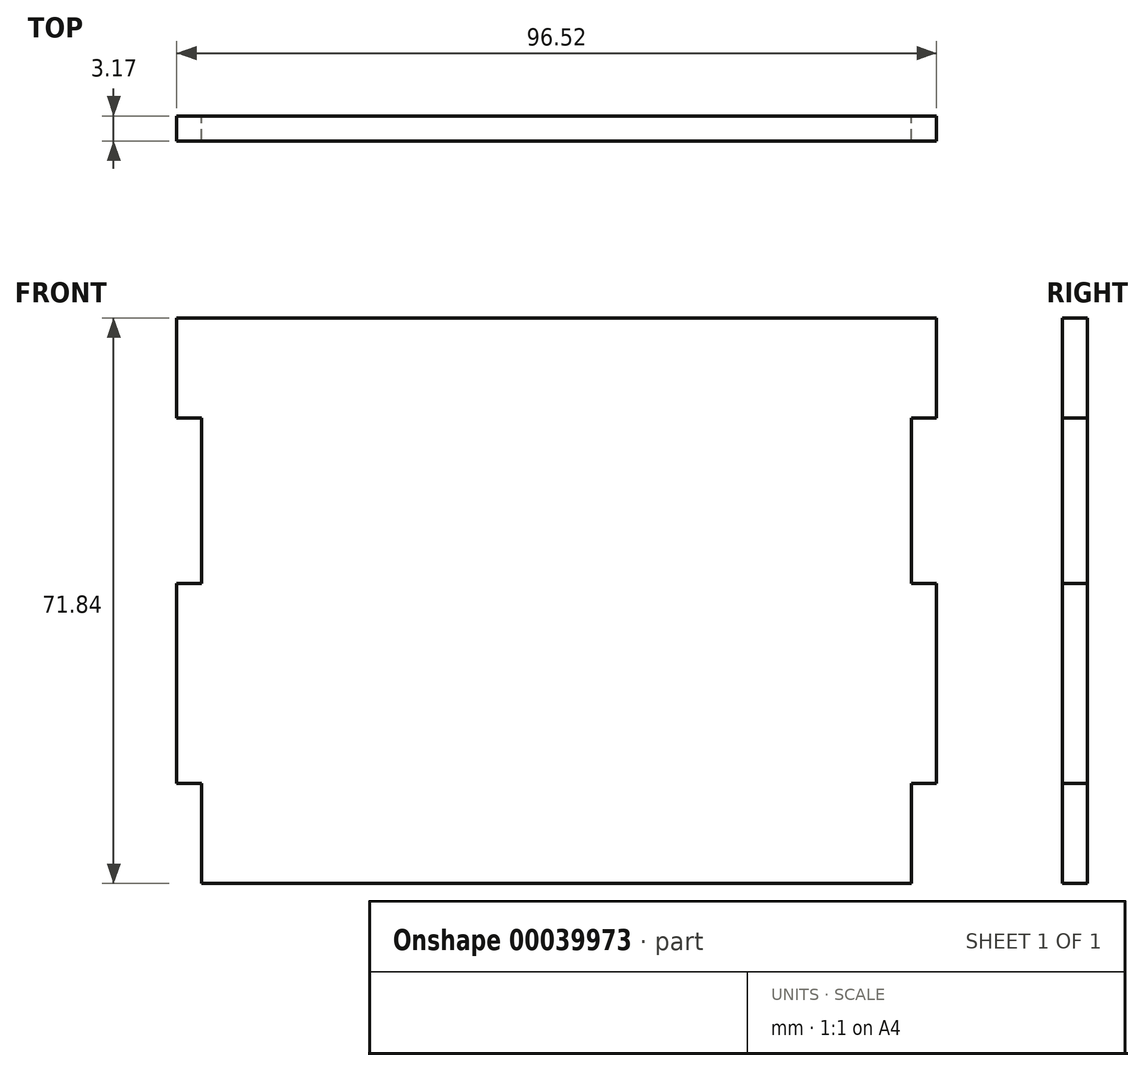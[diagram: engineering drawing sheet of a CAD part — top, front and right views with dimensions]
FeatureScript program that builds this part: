
annotation { "Feature Type Name" : "Feature", "Feature Type Description" : "" }
export const myFeature = defineFeature(function(context is Context, id is Id, definition is map)
    precondition{}
    {
        {
            var Q0;
            Q0=qCreatedBy(makeId("Front.planeOp"),FACE);
            var sketch = newSketch(context, id + "F0", { "sketchPlane" : qUnion([Q0])});
            skLineSegment(sketch, "E0.rect.bottom", {"start": v(48.26, -35.92) * mm, "end": v(-48.26, -35.92) * mm});
            skLineSegment(sketch, "E0.rect.top", {"start": v(48.26, 35.92) * mm, "end": v(-48.26, 35.92) * mm});
            skLineSegment(sketch, "E0.rect.left", {"start": v(48.26, -35.92) * mm, "end": v(48.26, 35.92) * mm});
            skLineSegment(sketch, "E0.rect.right", {"start": v(-48.26, -35.92) * mm, "end": v(-48.26, 35.92) * mm});
            skPoint(sketch, "E0.rect.middle", {"position": v(0, 0) * mm});
            skLineSegment(sketch, "E1", {"start": v(0, 35.92) * mm, "end": v(0, -37.02) * mm, "construction": true});
            skPoint(sketch, "E1.endSnap0", {"position": v(0, -35.92) * mm});
            skLineSegment(sketch, "E2", {"start": v(-48.26, -23.22) * mm, "end": v(-45.09, -23.22) * mm});
            skLineSegment(sketch, "E3", {"start": v(-48.26, 23.22) * mm, "end": v(-45.09, 23.22) * mm});
            skLineSegment(sketch, "E4", {"start": v(-45.09, 2.18) * mm, "end": v(-48.26, 2.18) * mm});
            skLineSegment(sketch, "E5", {"start": v(-45.09, 23.22) * mm, "end": v(-45.09, 2.18) * mm});
            skLineSegment(sketch, "E6", {"start": v(-45.09, -23.22) * mm, "end": v(-45.09, -35.92) * mm});
            skLineSegment(sketch, "E7.MirrorCS", {"start": v(48.26, 23.22) * mm, "end": v(45.09, 23.22) * mm});
            skLineSegment(sketch, "E8.MirrorCS", {"start": v(45.08, 23.22) * mm, "end": v(45.09, 2.18) * mm});
            skLineSegment(sketch, "E9.MirrorCS", {"start": v(48.26, -23.22) * mm, "end": v(45.09, -23.22) * mm});
            skLineSegment(sketch, "E10.MirrorCS", {"start": v(45.09, -23.22) * mm, "end": v(45.09, -35.92) * mm});
            skLineSegment(sketch, "E11.MirrorCS", {"start": v(45.09, 2.18) * mm, "end": v(48.26, 2.18) * mm});
            skSolve(sketch);
        }
        {
            var Q0;
            {var subQ2=sQuery(id+"F0.wireOp",EDGE,"E0.rect.top");Q0=makeQuery(id+"F0.imprint","IMPRINT",FACE,{"disambiguationData":[TD([[makeQuery(id+"F0.imprint","IMPRINT",EDGE,{"derivedFrom":subQ2}),1.0]])]});}
            extrude(context, id + "F1", {"entities" : qUnion([Q0]), "depth" : 3.17 * mm});
        }
    });
